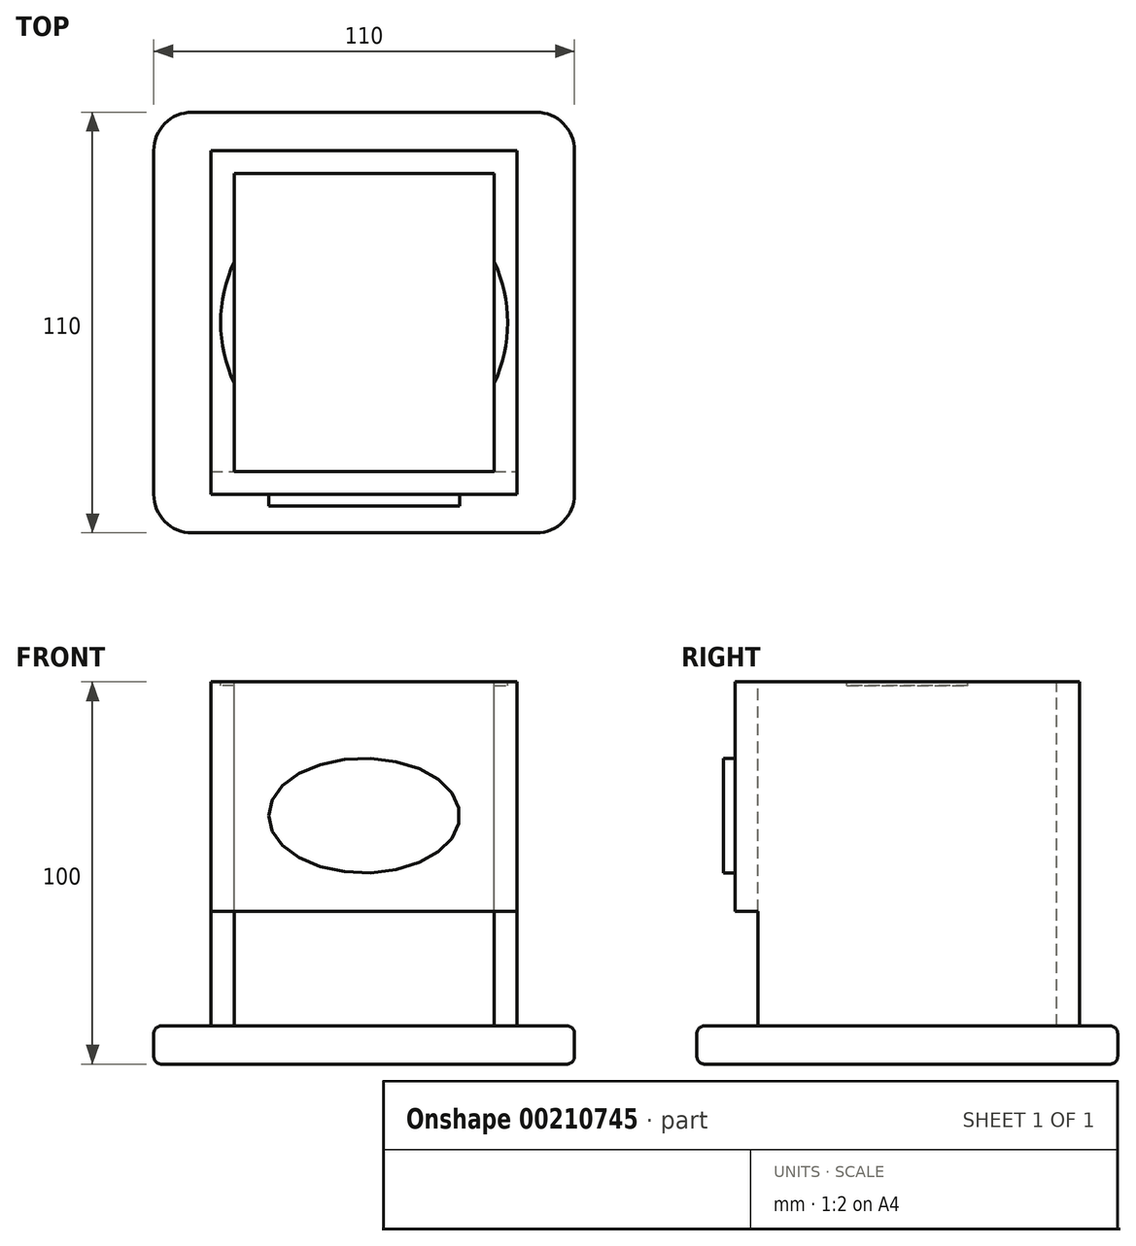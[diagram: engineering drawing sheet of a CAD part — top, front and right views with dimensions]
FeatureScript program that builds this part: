
annotation { "Feature Type Name" : "Feature", "Feature Type Description" : "" }
export const myFeature = defineFeature(function(context is Context, id is Id, definition is map)
    precondition{}
    {
        {
            var Q0;
            Q0=qCreatedBy(makeId("Top.planeOp"),FACE);
            var sketch = newSketch(context, id + "F0", { "sketchPlane" : qUnion([Q0])});
            skLineSegment(sketch, "E0.bottom", {"start": v(40, -45) * mm, "end": v(-40, -45) * mm});
            skLineSegment(sketch, "E0.top", {"start": v(40, 45) * mm, "end": v(-40, 45) * mm});
            skLineSegment(sketch, "E0.left", {"start": v(40, -45) * mm, "end": v(40, 45) * mm});
            skLineSegment(sketch, "E0.right", {"start": v(-40, -45) * mm, "end": v(-40, 45) * mm});
            skPoint(sketch, "E0.middle", {"position": v(0, 0) * mm});
            skSolve(sketch);
        }
        {
            var Q0;
            Q0 = qSketchRegion(id + "F0", true);
            extrude(context, id + "F1", {"entities" : qUnion([Q0]), "endBound" : BoundingType.SYMMETRIC, "depth" : 100 * mm});
        }
        {
            var Q0;
            Q0=qCreatedBy(makeId("Top.planeOp"),FACE);
            var sketch = newSketch(context, id + "F2", { "sketchPlane" : qUnion([Q0])});
            skLineSegment(sketch, "E1.bottom", {"start": v(34, 39) * mm, "end": v(-34, 39) * mm});
            skLineSegment(sketch, "E1.top", {"start": v(34, -39) * mm, "end": v(-34, -39) * mm});
            skLineSegment(sketch, "E1.left", {"start": v(34, 39) * mm, "end": v(34, -39) * mm});
            skLineSegment(sketch, "E1.right", {"start": v(-34, 39) * mm, "end": v(-34, -39) * mm});
            skPoint(sketch, "E1.middle", {"position": v(0, 0) * mm});
            skSolve(sketch);
        }
        {
            var Q0;
            Q0 = qSketchRegion(id + "F2", true);
            extrude(context, id + "F3", {"entities" : qUnion([Q0]), "operationType" : NewBodyOperationType.REMOVE, "endBound" : BoundingType.THROUGH_ALL, "oppositeDirection" : true, "depth" : 25 * mm, "hasSecondDirection" : true, "secondDirectionBound" : SecondDirectionBoundingType.THROUGH_ALL, "secondDirectionOppositeDirection" : false, "secondDirectionDepth" : 25 * mm});
        }
        {
            var Q0;
            Q0=makeQuery(id+"F1.opExtrude","CAP_FACE",FACE,{"disambiguationData":[OSD([sQuery(id+"F0.wireOp",EDGE,"E0.bottom"),sQuery(id+"F0.wireOp",EDGE,"E0.top"),sQuery(id+"F0.wireOp",EDGE,"E0.left"),sQuery(id+"F0.wireOp",EDGE,"E0.right")])],"isStart":true});
            var sketch = newSketch(context, id + "F4", { "sketchPlane" : qUnion([Q0])});
            skLineSegment(sketch, "E2.bottom", {"start": v(55, 55) * mm, "end": v(-55, 55) * mm});
            skLineSegment(sketch, "E2.top", {"start": v(55, -55) * mm, "end": v(-55, -55) * mm});
            skLineSegment(sketch, "E2.left", {"start": v(55, 55) * mm, "end": v(55, -55) * mm});
            skLineSegment(sketch, "E2.right", {"start": v(-55, 55) * mm, "end": v(-55, -55) * mm});
            skPoint(sketch, "E2.middle", {"position": v(0, 0) * mm});
            skSolve(sketch);
        }
        {
            var Q0;
            Q0 = qSketchRegion(id + "F4", true);
            extrude(context, id + "F5", {"entities" : qUnion([Q0]), "operationType" : NewBodyOperationType.ADD, "oppositeDirection" : true, "depth" : 10 * mm});
        }
        {
            var Q0;
            Q0=makeQuery(id+"F5.opExtrude","SWEPT_EDGE",EDGE,{"disambiguationData":[OSD([sQuery(id+"F4.wireOp",EDGE,"E2.bottom"),sQuery(id+"F4.wireOp",EDGE,"E2.left")])]});
            var Q1;
            Q1=makeQuery(id+"F5.opExtrude","SWEPT_EDGE",EDGE,{"disambiguationData":[OSD([sQuery(id+"F4.wireOp",EDGE,"E2.top"),sQuery(id+"F4.wireOp",EDGE,"E2.left")])]});
            var Q2;
            Q2=makeQuery(id+"F5.opExtrude","SWEPT_EDGE",EDGE,{"disambiguationData":[OSD([sQuery(id+"F4.wireOp",EDGE,"E2.bottom"),sQuery(id+"F4.wireOp",EDGE,"E2.right")])]});
            var Q3;
            Q3=makeQuery(id+"F5.opExtrude","SWEPT_EDGE",EDGE,{"disambiguationData":[OSD([sQuery(id+"F4.wireOp",EDGE,"E2.top"),sQuery(id+"F4.wireOp",EDGE,"E2.right")])]});
            fillet(context, id + "F6", {"entities" : qUnion([Q0, Q1, Q2, Q3]), "radius" : 10 * mm, "tangentPropagation" : true, "allowEdgeOverflow" : false});
        }
        {
            var Q0;
            Q0=makeQuery(id+"F5.opExtrude","CAP_EDGE",EDGE,{"disambiguationData":[OSD([sQuery(id+"F4.wireOp",EDGE,"E2.bottom")])],"isStart":false});
            var Q1;
            Q1=makeQuery(id+"F5.opExtrude","CAP_EDGE",EDGE,{"disambiguationData":[OSD([sQuery(id+"F4.wireOp",EDGE,"E2.bottom")])],"isStart":true});
            fillet(context, id + "F7", {"entities" : qUnion([Q0, Q1]), "radius" : 2 * mm, "tangentPropagation" : true, "allowEdgeOverflow" : false});
        }
        {
            var Q0;
            Q0=makeQuery(id+"F1.opExtrude","SWEPT_FACE",FACE,{"disambiguationData":[OSD([sQuery(id+"F0.wireOp",EDGE,"E0.bottom")])]});
            var sketch = newSketch(context, id + "F8", { "sketchPlane" : qUnion([Q0])});
            skLineSegment(sketch, "E3.bottom", {"start": v(-40, -40) * mm, "end": v(40, -40) * mm});
            skLineSegment(sketch, "E3.top", {"start": v(-40, -10) * mm, "end": v(40, -10) * mm});
            skLineSegment(sketch, "E3.left", {"start": v(-40, -40) * mm, "end": v(-40, -10) * mm});
            skLineSegment(sketch, "E3.right", {"start": v(40, -40) * mm, "end": v(40, -10) * mm});
            skSolve(sketch);
        }
        {
            var Q0;
            Q0 = qSketchRegion(id + "F8", true);
            extrude(context, id + "F9", {"entities" : qUnion([Q0]), "operationType" : NewBodyOperationType.REMOVE, "oppositeDirection" : true, "depth" : 6 * mm});
        }
        {
            var Q0;
            Q0=makeQuery(id+"FITUqqcnNrqaom9_1.1.F5.boolean.opBoolean","MERGE",FACE,{"derivedFrom":[makeQuery(id+"F1.opExtrude","CAP_FACE",FACE,{"disambiguationData":[OSD([sQuery(id+"F0.wireOp",EDGE,"E0.bottom"),sQuery(id+"F0.wireOp",EDGE,"E0.top"),sQuery(id+"F0.wireOp",EDGE,"E0.left"),sQuery(id+"F0.wireOp",EDGE,"E0.right")])],"isStart":false}),makeQuery(id+"FITUqqcnNrqaom9_1.1.F5.opExtrude","CAP_FACE",FACE,{"disambiguationData":[OSD([sQuery(id+"F4.wireOp",EDGE,"E2.bottom"),sQuery(id+"F4.wireOp",EDGE,"E2.top"),sQuery(id+"F4.wireOp",EDGE,"E2.left"),sQuery(id+"F4.wireOp",EDGE,"E2.right")])],"isStart":true})]});
            var sketch = newSketch(context, id + "F10", { "sketchPlane" : qUnion([Q0])});
            skCircle(sketch, "E4", {"center": v(0, 0) * mm, "radius": 37.5 * mm});
            skSolve(sketch);
        }
        {
            var Q0;
            Q0 = qSketchRegion(id + "F10", true);
            extrude(context, id + "F11", {"entities" : qUnion([Q0]), "operationType" : NewBodyOperationType.REMOVE, "oppositeDirection" : true, "depth" : 1 * mm});
        }
        {
            var Q0;
            Q0=makeQuery(id+"F11.boolean.opBoolean","COPY",FACE,{"derivedFrom":makeQuery(id+"F11.opExtrude","CAP_FACE",FACE,{"disambiguationData":[OSD([sQuery(id+"F10.wireOp",EDGE,"E4")])],"isStart":false})});
            var sketch = newSketch(context, id + "F12", { "sketchPlane" : qUnion([Q0])});
            skCircle(sketch, "E5", {"center": v(0, 0) * mm, "radius": 16 * mm});
            skSolve(sketch);
        }
        {
            var Q0;
            Q0 = qSketchRegion(id + "F12", true);
            extrude(context, id + "F13", {"entities" : qUnion([Q0]), "operationType" : NewBodyOperationType.REMOVE, "endBound" : BoundingType.UP_TO_NEXT, "oppositeDirection" : true, "depth" : 25 * mm});
        }
        {
            var Q0;
            Q0=makeQuery(id+"F1.opExtrude","SWEPT_FACE",FACE,{"disambiguationData":[OSD([sQuery(id+"F0.wireOp",EDGE,"E0.bottom")])]});
            var sketch = newSketch(context, id + "F14", { "sketchPlane" : qUnion([Q0])});
            skEllipse(sketch, "E6", {"center": v(0, 15) * mm, "majorRadius": 15 * mm, "minorRadius": 25 * mm, "majorAxis": v(0, 1)});
            skSolve(sketch);
        }
        {
            var Q0;
            Q0 = qSketchRegion(id + "F14", true);
            extrude(context, id + "F15", {"entities" : qUnion([Q0]), "operationType" : NewBodyOperationType.ADD, "depth" : 3 * mm});
        }
    });
